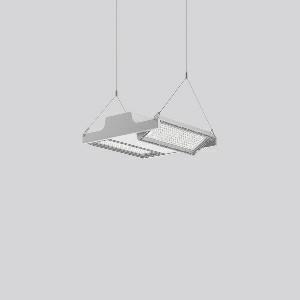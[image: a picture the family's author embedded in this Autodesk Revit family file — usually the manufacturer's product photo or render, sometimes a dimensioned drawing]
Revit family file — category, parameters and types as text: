
# Revit family: light_case_921681_004_76_de7f
name_source: partatom
category: Lighting Fixtures
units: mm (PartAtom-declared; Revit-internal decimal feet)

## family parameters
Cut with Voids When Loaded = No
Host = Face
Light Source = No
Part Type = Normal
Room Calculation Point = No
Round Connector Dimension = Use Diameter
Shared = No

## types (1)
- LIGHT CASE (1 x LED Modul 840, 8850 lm, 4000)
    Apparent Load = 117 VA
    CIE Flux Codes = 85 97 100 100 100
    Color Rendering = 80
    Color Temperature = 4000
    Default Elevation = 1800 mm
    Description = Series: LIGHT CASE
Flat highbay luminaire for chain or cable suspension with 2 LED modules that can be swivelled. Housing: die cast aluminium and sheet steel, powder-coated. Optimised thermal management thanks to special luminaire design. Self-cleaning heat sink for constant heat dissipation. Cover: plastic (polycarbonate, shockproof), with integrated four-row lens system. LED modules can be swivelled ± 30° for optimum illumination. Suitable for chain or steel cable suspension (to be provided on site). With 5-pin connection terminal (1.5 m). With integrated movement sensor and light sensor for daylight detection on request. Ball impact proof in accordance with DIN 18032-03 (except steel cable suspension). Luminaire with limited surface temperature in accordance with EN 60598-2-24 for use in environments in which a deposit of conductive dust on the luminaire can be expected. 
Colour: silver, matt (approx. RAL 9006)
Length: 406 mm
Width: 397 mm
Height: 110 mm
Lamp: LED
Socket: without socket
Colour temperature: 4000K
Colour rendering index (CRI): 80
System power: 117 W
Rated luminous flux: 17700 lm
Luminous efficiency: 151 lm/W
Control gear: Converter, dimmable, DALI
Protection class: I
Type of protection: IP 65
    Height = 110 mm
    Lamp = 1 x LED Modul 840
    Lamp Light Flux = 8850 lm
    Lamp count = 1
    Length = 406 mm
    Lifetime = 50000 h
    Luminous efficacy = 151 lm/W
    Manufacturer = RZB
    ModVariant = No
    Model = 921681.004.76
    Mounting Place = Ceiling
    Mounting Type = Pendant
    Number of Poles = 1
    OnlyDefault = Yes
    Power Factor = 1
    Product Name = LIGHT CASE
    Product group = Pendant commercial luminaires
    ProductGroupID = 903
    Protection Class = Protection class I
    Protection Degree = IP 65
    RLX_Detail_Level = 1
    RLX_Emergency_Light_Flux = 0 lm
    RLX_Emergency_Type = 0
    RLX_Emergency_Type_DB = No
    RlxData = <blob elided: 26033 chars, md5=09219f66>
    Socket = socket
    Standby Power = 0 W
    System Light Flux = 17700 lm
    System Power = 117 W
    Type Comments = Product without accessories
    Type Image = 921517.004.76.jpg
    URL = http://relux.com
    VarID = ---
    Voltage = 230 V
    Voltage Range = 220-240 V
    Weight = 0.00 kg
    Width = 397 mm

## geometry (parser evidence)
native form markers: Blend x4, Sweep x17
no freeform markers — native parametric forms only
